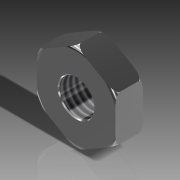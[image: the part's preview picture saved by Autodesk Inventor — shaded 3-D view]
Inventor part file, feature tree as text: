
AUTODESK INVENTOR PART (.ipt)
format: ipt  version: 2014 SP1 (Build 180222100, 222)  size: 150,016 bytes
history: native  units: in
note: dims shown in document units (in); Inventor stores cm internally (conversion verified against a paired STEP export)
features: other x1, imported_body x1, thread x1
ambient origin geometry x8: Origin, YZ Plane, XZ Plane, XY Plane, X Axis, Y Axis, Z Axis, Center Point
bodies: Body1 (feature_tree)
feature tree (3):
  parser-record x1  (decoder bookkeeping rows leaked as tree rows — omitted from the tree; the rows remain in map.json)
  imported_body  "Base1"
  thread  "Thread1"  [1 undecoded]
note: 1 required parameter value undecoded (feature->parameter linkage not recoverable at this tier; creation-order binding heuristic only, values carry confidence <= 0.55)
